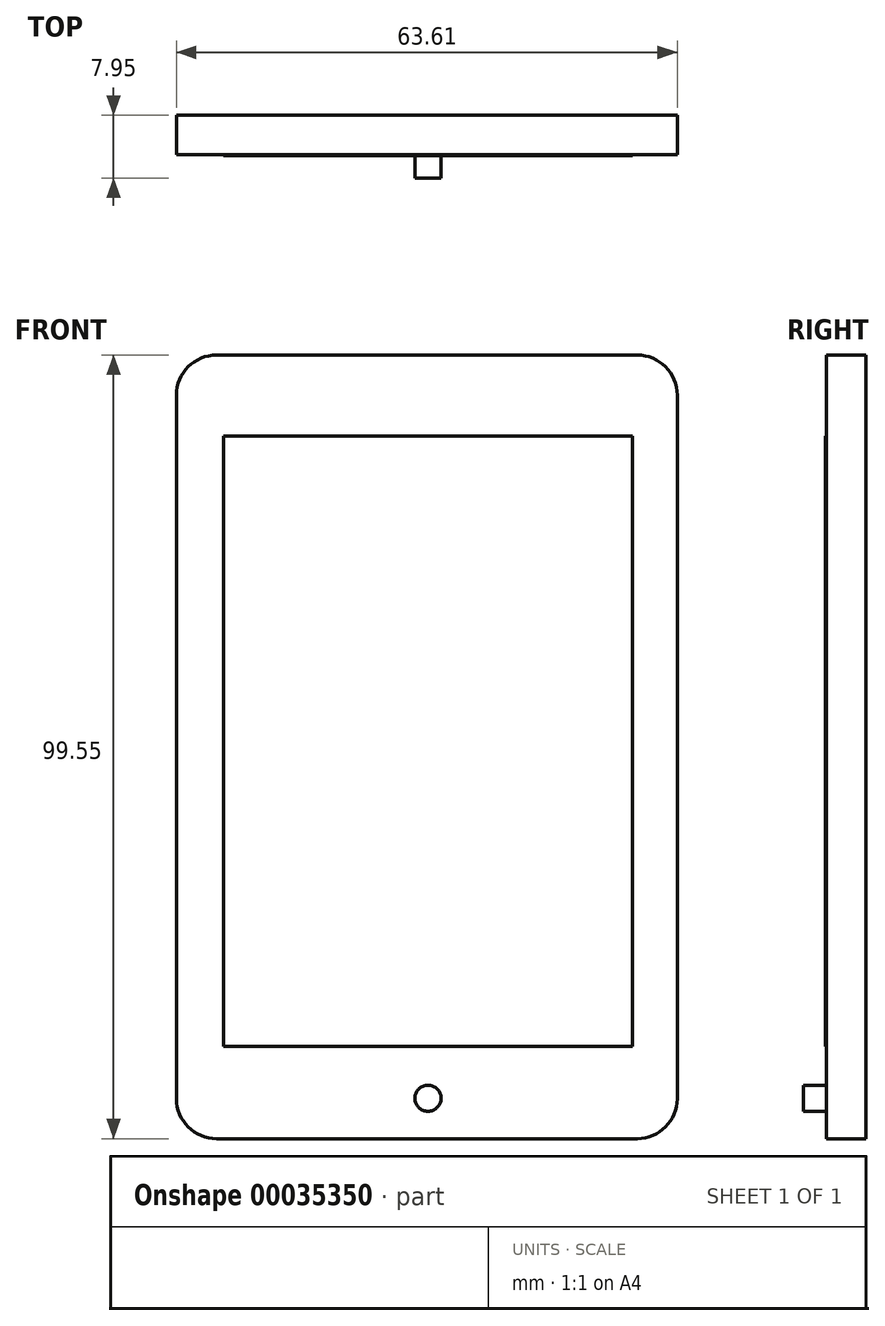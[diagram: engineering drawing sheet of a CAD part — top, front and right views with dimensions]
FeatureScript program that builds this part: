
annotation { "Feature Type Name" : "Feature", "Feature Type Description" : "" }
export const myFeature = defineFeature(function(context is Context, id is Id, definition is map)
    precondition{}
    {
        {
            var Q0;
            Q0=qCreatedBy(makeId("Front.planeOp"),FACE);
            var sketch = newSketch(context, id + "F0", { "sketchPlane" : qUnion([Q0])});
            skLineSegment(sketch, "E0.bottom", {"start": v(-31.95, 42.36) * mm, "end": v(31.66, 42.36) * mm});
            skLineSegment(sketch, "E0.top", {"start": v(-31.95, -57.2) * mm, "end": v(31.66, -57.2) * mm});
            skLineSegment(sketch, "E0.left", {"start": v(-31.95, 42.36) * mm, "end": v(-31.95, -57.2) * mm});
            skLineSegment(sketch, "E0.right", {"start": v(31.66, 42.36) * mm, "end": v(31.66, -57.2) * mm});
            skSolve(sketch);
        }
        {
            var Q0;
            Q0=makeQuery(id+"F0.imprint","IMPRINT",FACE,{"disambiguationData":[TD([[makeQuery(id+"F0.imprint","IMPRINT",EDGE,{"derivedFrom":sQuery(id+"F0.wireOp",EDGE,"E0.bottom")}),-1.0]])]});
            var sketch = newSketch(context, id + "F1", { "sketchPlane" : qUnion([Q0])});
            skLineSegment(sketch, "E1.bottom", {"start": v(-25.96, 32.09) * mm, "end": v(25.96, 32.09) * mm});
            skLineSegment(sketch, "E1.top", {"start": v(-25.96, -45.5) * mm, "end": v(25.96, -45.5) * mm});
            skLineSegment(sketch, "E1.left", {"start": v(-25.96, 32.09) * mm, "end": v(-25.96, -45.5) * mm});
            skLineSegment(sketch, "E1.right", {"start": v(25.96, 32.09) * mm, "end": v(25.96, -45.5) * mm});
            skSolve(sketch);
        }
        {
            var Q0;
            Q0=makeQuery(id+"F0.imprint","IMPRINT",FACE,{"disambiguationData":[TD([[makeQuery(id+"F0.imprint","IMPRINT",EDGE,{"derivedFrom":sQuery(id+"F0.wireOp",EDGE,"E0.bottom")}),-1.0]])]});
            extrude(context, id + "F2", {"entities" : qUnion([Q0]), "oppositeDirection" : true, "depth" : 7.95 * mm});
        }
        {
            var Q0;
            Q0=makeQuery(id+"F2.opExtrude","SWEPT_EDGE",EDGE,{"disambiguationData":[OSD([sQuery(id+"F0.wireOp",EDGE,"E0.bottom"),sQuery(id+"F0.wireOp",EDGE,"E0.left")])]});
            fillet(context, id + "F3", {"entities" : qUnion([Q0]), "radius" : 5.08 * mm, "tangentPropagation" : true, "allowEdgeOverflow" : false});
        }
        {
            var Q0;
            Q0=makeQuery(id+"F2.opExtrude","SWEPT_EDGE",EDGE,{"disambiguationData":[OSD([sQuery(id+"F0.wireOp",EDGE,"E0.bottom"),sQuery(id+"F0.wireOp",EDGE,"E0.right")])]});
            fillet(context, id + "F4", {"entities" : qUnion([Q0]), "radius" : 5.08 * mm, "tangentPropagation" : true, "allowEdgeOverflow" : false});
        }
        {
            var Q0;
            Q0=makeQuery(id+"F2.opExtrude","SWEPT_EDGE",EDGE,{"disambiguationData":[OSD([sQuery(id+"F0.wireOp",EDGE,"E0.top"),sQuery(id+"F0.wireOp",EDGE,"E0.right")])]});
            fillet(context, id + "F5", {"entities" : qUnion([Q0]), "radius" : 5.08 * mm, "tangentPropagation" : true, "allowEdgeOverflow" : false});
        }
        {
            var Q0;
            Q0=makeQuery(id+"F2.opExtrude","SWEPT_EDGE",EDGE,{"disambiguationData":[OSD([sQuery(id+"F0.wireOp",EDGE,"E0.top"),sQuery(id+"F0.wireOp",EDGE,"E0.left")])]});
            fillet(context, id + "F6", {"entities" : qUnion([Q0]), "radius" : 5.08 * mm, "tangentPropagation" : true, "allowEdgeOverflow" : false});
        }
        {
            var Q0;
            Q0=makeQuery(id+"F1.imprint","IMPRINT",FACE,{"disambiguationData":[TD([[makeQuery(id+"F1.imprint","IMPRINT",EDGE,{"derivedFrom":sQuery(id+"F1.wireOp",EDGE,"E1.bottom")}),1.0]])]});
            var sketch = newSketch(context, id + "F7", { "sketchPlane" : qUnion([Q0])});
            skCircle(sketch, "E2", {"center": v(0, -52.06) * mm, "radius": 4.08 * mm});
            skSolve(sketch);
        }
        {
            var Q0;
            Q0=makeQuery(id+"F1.imprint","IMPRINT",FACE,{"disambiguationData":[TD([[makeQuery(id+"F1.imprint","IMPRINT",EDGE,{"derivedFrom":sQuery(id+"F1.wireOp",EDGE,"E1.bottom")}),1.0]])]});
            var sketch = newSketch(context, id + "F8", { "sketchPlane" : qUnion([Q0])});
            skCircle(sketch, "E3", {"center": v(0, -52.06) * mm, "radius": 1.66 * mm});
            skSolve(sketch);
        }
        {
            var Q0;
            Q0=makeQuery(id+"F8.imprint","IMPRINT",FACE,{"disambiguationData":[TD([[makeQuery(id+"F8.imprint","IMPRINT",EDGE,{"derivedFrom":sQuery(id+"F8.wireOp",EDGE,"E3")}),-1.0]])]});
            extrude(context, id + "F9", {"entities" : qUnion([Q0]), "operationType" : NewBodyOperationType.REMOVE, "oppositeDirection" : true, "depth" : 2.96 * mm});
        }
        {
            var Q0;
            Q0=makeQuery(id+"F1.imprint","IMPRINT",FACE,{"disambiguationData":[TD([[makeQuery(id+"F1.imprint","IMPRINT",EDGE,{"derivedFrom":sQuery(id+"F1.wireOp",EDGE,"E1.bottom")}),-1.0]])]});
            extrude(context, id + "F10", {"entities" : qUnion([Q0]), "operationType" : NewBodyOperationType.REMOVE, "oppositeDirection" : true, "depth" : 2.82 * mm});
        }
    });
